FCSTD DOCUMENT  (FreeCAD 0.19R0.19.2)
Label: 004
License: All rights reserved
LicenseURL: http://en.wikipedia.org/wiki/All_rights_reserved
objects: Sketcher::SketchObject×1
note: 1 computed .brp shape members not serialized (recipe doc carries the construction recipe); baked Part::Feature solids carry a one-line shape summary decoded from their .brp

FEATURE [Sketcher::SketchObject] Sketch
  FullyConstrained = true
  sketch-geometry (20):
    g0: ArcOfCircle CenterX=-3.45031e-07 CenterY=5e-07 CenterZ=0 NormalX=0 NormalY=0 NormalZ=1 AngleXU=0 Radius=10.2 StartAngle=5.4126 EndAngle=7.15377
    g1: ArcOfCircle CenterX=-3.45031e-07 CenterY=5e-07 CenterZ=0 NormalX=0 NormalY=0 NormalZ=1 AngleXU=0 Radius=10.2 StartAngle=2.27101 EndAngle=4.01218
    g2: LineSegment StartX=-6.57267 StartY=7.8 StartZ=0 EndX=6.57267 EndY=7.8 EndZ=0
    g3: LineSegment StartX=-6.57267 StartY=-7.8 StartZ=0 EndX=6.57267 EndY=-7.8 EndZ=0
    g4: ArcOfCircle CenterX=-3.45031e-07 CenterY=5e-07 CenterZ=0 NormalX=0 NormalY=0 NormalZ=1 AngleXU=0 Radius=11.6 StartAngle=2.27101 EndAngle=4.01218
    g5: ArcOfCircle CenterX=-3.45031e-07 CenterY=5e-07 CenterZ=0 NormalX=0 NormalY=0 NormalZ=1 AngleXU=0 Radius=11.6 StartAngle=5.4126 EndAngle=7.15377
    g6: LineSegment StartX=-7.4748 StartY=8.87059 StartZ=0 EndX=7.4748 EndY=8.87059 EndZ=0
    g7: LineSegment StartX=-7.4748 StartY=-8.87059 StartZ=0 EndX=7.4748 EndY=-8.87059 EndZ=0
    g8: LineSegment StartX=-3.45031e-07 StartY=2.5 StartZ=0 EndX=-3.45031e-07 EndY=5e-07 EndZ=0
    g9: LineSegment StartX=-3.45031e-07 StartY=5e-07 StartZ=0 EndX=-3.45031e-07 EndY=-2.5 EndZ=0
    g10: LineSegment StartX=-3.45031e-07 StartY=2.5 StartZ=0 EndX=-3.45031e-07 EndY=3.9 EndZ=0
    g11: LineSegment StartX=-3.45031e-07 StartY=-2.5 StartZ=0 EndX=-3.45031e-07 EndY=-3.9 EndZ=0
    g12: LineSegment StartX=-3.45031e-07 StartY=2.5 StartZ=0 EndX=-30.2 EndY=2.5 EndZ=0
    g13: LineSegment StartX=-3.45031e-07 StartY=-2.5 StartZ=0 EndX=-30.2 EndY=-2.5 EndZ=0
    g14: LineSegment StartX=-3.45031e-07 StartY=2.5 StartZ=0 EndX=30.2 EndY=2.5 EndZ=0
    g15: LineSegment StartX=-3.45031e-07 StartY=-2.5 StartZ=0 EndX=30.2 EndY=-2.5 EndZ=0
    g16: LineSegment StartX=-3.45031e-07 StartY=-3.9 StartZ=0 EndX=10.9247 EndY=-3.9 EndZ=0
    g17: LineSegment StartX=-3.45031e-07 StartY=-3.9 StartZ=0 EndX=-10.9247 EndY=-3.9 EndZ=0
    g18: LineSegment StartX=-3.45031e-07 StartY=3.9 StartZ=0 EndX=-10.9247 EndY=3.9 EndZ=0
    g19: LineSegment StartX=-3.45031e-07 StartY=3.9 StartZ=0 EndX=10.9247 EndY=3.9 EndZ=0
  constraints (57):
    c: Block(g0)
    c: Equal(g0,g1)
    c: Coincident(g0,g1)
    c: Coincident(g2,g1)
    c: Coincident(g2,g0)
    c: Horizontal(g2)
    c: Coincident(g3,g1)
    c: Coincident(g3,g0)
    c: Horizontal(g3)
    c: Block(g2)
    c: Block(g3)
    c: Coincident(g4,g0)
    c: Coincident(g5,g0)
    c: Block(g5)
    c: Block(g4)
    c: Coincident(g6,g4)
    c: Coincident(g6,g5)
    c: Horizontal(g6)
    c: Coincident(g7,g4)
    c: Coincident(g7,g5)
    c: Horizontal(g7)
    c: Distance(g8) = 2.5
    c: Vertical(g8)
    c: Coincident(g0,g8)
    c: Vertical(g9)
    c: Distance(g9) = 2.5
    c: Coincident(g9,g0)
    c: Vertical(g10)
    c: Distance(g10) = 1.4
    c: Vertical(g11)
    c: Distance(g11) = 1.4
    c: Coincident(g10,g8)
    c: Coincident(g11,g9)
    c: Coincident(g12,g8)
    c: Horizontal(g12)
    c: Distance(g12) = 30.2
    c: Horizontal(g13)
    c: Equal(g12,g13) = 30.2
    c: Coincident(g13,g9)
    c: Coincident(g14,g8)
    c: Horizontal(g14)
    c: Distance(g14) = 30.2
    c: Horizontal(g15)
    c: Equal(g14,g15) = 30.2
    c: Coincident(g15,g9)
    c: Coincident(g16,g11)
    c: PointOnObject(g16,g5)
    c: Horizontal(g16)
    c: Coincident(g17,g11)
    c: PointOnObject(g17,g4)
    c: Horizontal(g17)
    c: Coincident(g18,g10)
    c: PointOnObject(g18,g4)
    c: Horizontal(g18)
    c: Coincident(g19,g10)
    c: PointOnObject(g19,g5)
    c: Horizontal(g19)
